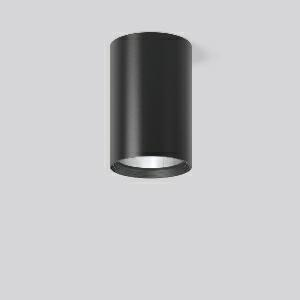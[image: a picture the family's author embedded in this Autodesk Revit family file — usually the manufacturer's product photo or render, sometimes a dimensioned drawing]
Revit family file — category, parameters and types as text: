
# Revit family: heledon_maxi_a_931218_003_1_76_568b
name_source: partatom
category: Lighting Fixtures
units: mm (PartAtom-declared; Revit-internal decimal feet)

## family parameters
Cut with Voids When Loaded = No
Host = Face
Light Source = No
Part Type = Normal
Room Calculation Point = No
Round Connector Dimension = Use Diameter
Shared = No

## types (1)
- HELEDON maxi A (1 x LED Modul 940, 3500 lm, 4000)
    Apparent Load = 25 VA
    Approval mark = CE
    CIE Flux Codes = 100 100 100 100 100
    Color Rendering = 92
    Color Temperature = 4000
    Default Elevation = 1800 mm
    Description = Series: HELEDON maxi
Cylindrical surface-mounted downlight. Housing: die-cast aluminium, powder-coated. Internal ceiling frame polycarbonate with bayonet mounting. Black plastic ring and recessed LED to prevent glare from the side. Optical assembly with reflector made of MIRO-Silver with 98% total light reflection for outstanding efficiency - can be changed without tools. Best colour rendering index Ra>90. Suitable for Ceiling mounting. Easy installation with a separate ceiling frame with bayonet mounting and plug connection. Driver integrated. Connected via plug-in connector. High quality converter without flickering and stroboscopic effect. The following accessories can be mounted without use of tools: interchangeable lenses, decorative glasses, honeycomb louvre, clear and frosted diffusers, white interchangeable plastic ring. 
Colour: deep black, matt (RAL 9005)
Diameter: 123 mm
Height: 183 mm
Lamp: LED
Socket: without socket
Colour temperature: 4000K
Colour rendering index (CRI): 92
System power: 25 W
Rated luminous flux: 3500 lm
Luminous efficiency: 140 lm/W
Control gear: Converter, dimmable, DALI
Protection class: I
Type of protection: IP 20
    Height = 183 mm
    Lamp = 1 x LED Modul 940
    Lamp Light Flux = 3500 lm
    Lamp count = 1
    Length = 123 mm
    Lifetime = 50000 h
    Luminous efficacy = 140 lm/W
    Manufacturer = RZB
    ModVariant = No
    Model = 931218.003.1.76
    Mounting Place = Ceiling
    Mounting Type = Surface mounted
    Number of Poles = 1
    OnlyDefault = Yes
    Power Factor = 1
    Product Name = HELEDON maxi A
    Product group = Surface mounted downlights
    ProductGroupID = 302
    Protection Class = Protection class I
    Protection Degree = IP 20
    RLX_Detail_Level = 1
    RLX_Emergency_Light_Flux = 0 lm
    RLX_Emergency_Type = 0
    RLX_Emergency_Type_DB = No
    RlxData = <blob elided: 100345 chars, md5=72ee5974>
    Socket = socket
    Standby Power = 0 W
    System Light Flux = 3500 lm
    System Power = 25 W
    Type Comments = Product without accessories
    Type Image = 931192.003.jpg
    URL = http://relux.com
    VarID = ---
    Voltage = 230 V
    Voltage Range = 220-240 V
    Weight = 0.00 kg
    Width = 0 mm  [stored 0 ft]

note: [stored X ft] marks values corroborated as IEEE doubles in the binary element streams (Revit-internal decimal feet)

## geometry (parser evidence)
native form markers: Blend x4, Sweep x11
no freeform markers — native parametric forms only
